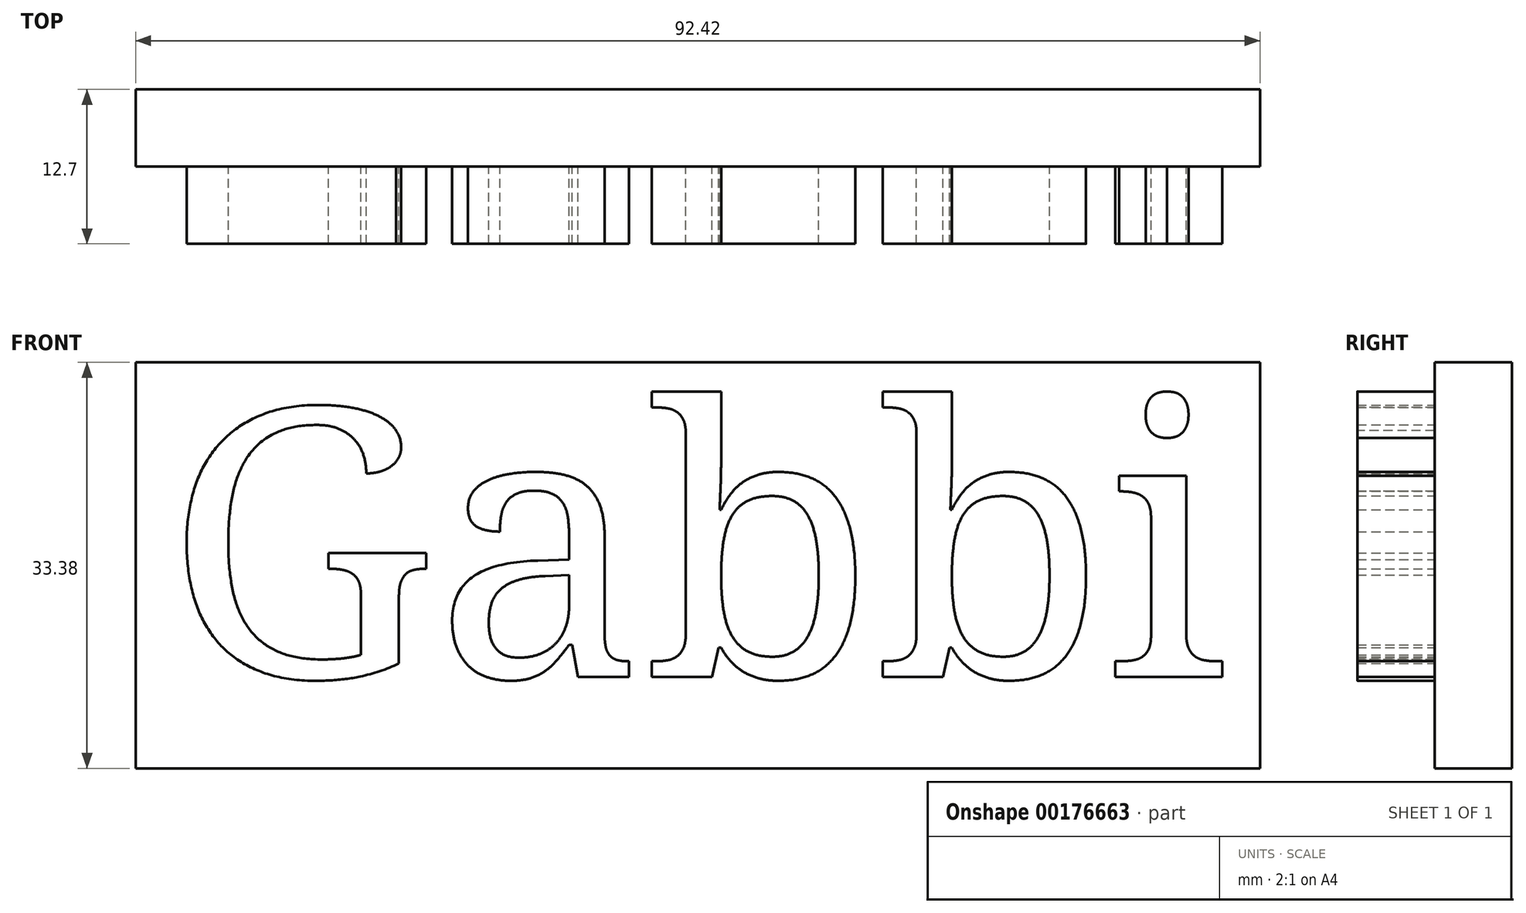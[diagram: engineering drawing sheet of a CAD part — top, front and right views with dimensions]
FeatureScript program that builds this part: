
annotation { "Feature Type Name" : "Feature", "Feature Type Description" : "" }
export const myFeature = defineFeature(function(context is Context, id is Id, definition is map)
    precondition{}
    {
        {
            var Q0;
            Q0=qCreatedBy(makeId("Front.planeOp"),FACE);
            var sketch = newSketch(context, id + "F0", { "sketchPlane" : qUnion([Q0])});
            skLineSegment(sketch, "E0.bottom", {"start": v(46.2, -16.69) * mm, "end": v(-46.2, -16.69) * mm});
            skLineSegment(sketch, "E0.top", {"start": v(46.2, 16.69) * mm, "end": v(-46.2, 16.69) * mm});
            skLineSegment(sketch, "E0.left", {"start": v(46.2, -16.69) * mm, "end": v(46.2, 16.69) * mm});
            skLineSegment(sketch, "E0.right", {"start": v(-46.2, -16.69) * mm, "end": v(-46.2, 16.69) * mm});
            skPoint(sketch, "E0.middle", {"position": v(0, 0) * mm});
            skSolve(sketch);
        }
        {
            var Q0;
            Q0=makeQuery(id+"F0.imprint","IMPRINT",FACE,{"disambiguationData":[TD([[makeQuery(id+"F0.imprint","IMPRINT",EDGE,{"derivedFrom":sQuery(id+"F0.wireOp",EDGE,"E0.bottom")}),-1.0]])]});
            extrude(context, id + "F1", {"entities" : qUnion([Q0]), "depth" : 6.35 * mm});
        }
        {
            var Q0;
            Q0=makeQuery(id+"F1.opExtrude","CAP_FACE",FACE,{"disambiguationData":[OSD([sQuery(id+"F0.wireOp",EDGE,"E0.bottom"),sQuery(id+"F0.wireOp",EDGE,"E0.top"),sQuery(id+"F0.wireOp",EDGE,"E0.left"),sQuery(id+"F0.wireOp",EDGE,"E0.right")])],"isStart":false});
            var sketch = newSketch(context, id + "F2", { "sketchPlane" : qUnion([Q0])});
            skText(sketch, "E1", { "text": "Gabbi", "fontName": "NotoSerif-Regular.ttf"});
            const initialGuessF2  = {"E1": [-0.04379, -0.00919, 1, 0, 0.02225]};
            skSetInitialGuess(sketch, initialGuessF2);
            skSolve(sketch);
        }
        {
            var Q0;
            Q0 = qSketchRegion(id + "F2", true);
            extrude(context, id + "F3", {"entities" : qUnion([Q0]), "operationType" : NewBodyOperationType.ADD, "depth" : 6.35 * mm});
        }
    });
